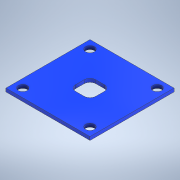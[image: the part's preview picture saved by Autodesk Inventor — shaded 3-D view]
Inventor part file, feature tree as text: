
AUTODESK INVENTOR PART (.ipt)
format: ipt  version: 2021 (Build 250183000, 183)  size: 137,216 bytes
history: native  units: mm
features: extrude x1, fillet x1, sketch x1
ambient origin geometry x8: Origin, YZ Plane, XZ Plane, XY Plane, X Axis, Y Axis, Z Axis, Center Point
bodies: Solid1 (feature_tree)
feature tree (3):
  extrude  "Extrusion1"  Depth=50.0mm
  fillet  "Fillet1"  Radius=12.0mm
  sketch  "Sketch1"  dims[d0=50.0mm d1=50.0mm d2=12.0mm d3=12.0mm d4=40.0mm d5=40.0mm d6=5.25mm d7=5.25mm d8=5.25mm d9=5.25mm d10=2.0mm d11=0.0mm d12=3.5mm]
